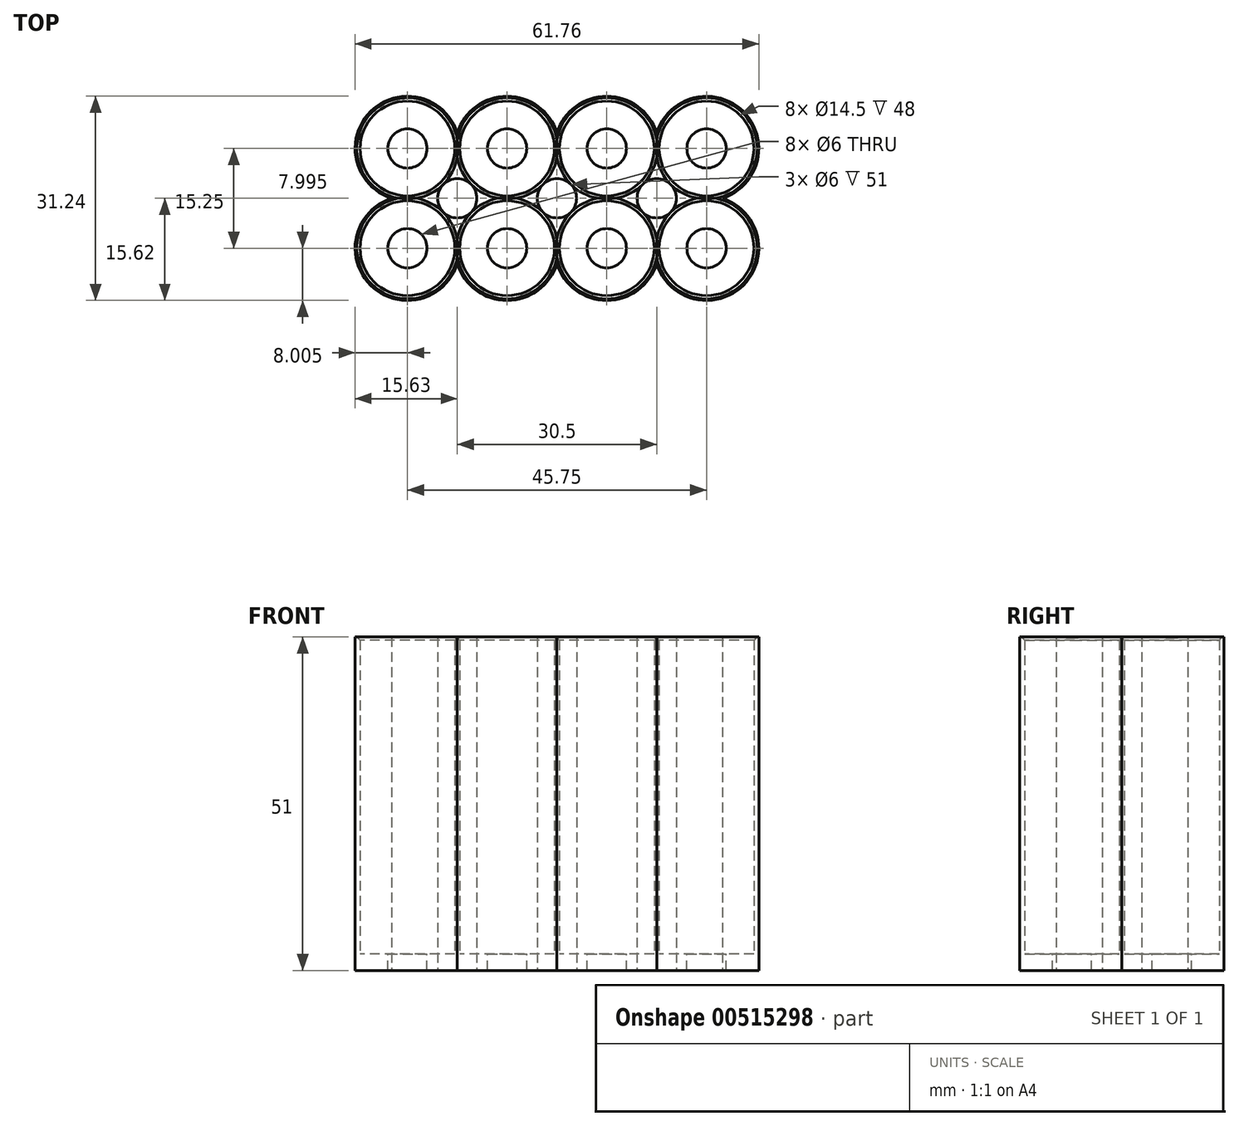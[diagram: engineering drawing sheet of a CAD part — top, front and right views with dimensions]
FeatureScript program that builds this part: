
annotation { "Feature Type Name" : "Feature", "Feature Type Description" : "" }
export const myFeature = defineFeature(function(context is Context, id is Id, definition is map)
    precondition{}
    {
        {
            var Q0;
            Q0=qCreatedBy(makeId("Top.planeOp"),FACE);
            var sketch = newSketch(context, id + "F0", { "sketchPlane" : qUnion([Q0])});
            skCircle(sketch, "E0", {"center": v(-7.62, 7.62) * mm, "radius": 7.25 * mm});
            skCircle(sketch, "E1", {"center": v(-22.88, 7.62) * mm, "radius": 7.25 * mm});
            skCircle(sketch, "E2.MirrorC", {"center": v(-7.62, -7.62) * mm, "radius": 7.25 * mm});
            skCircle(sketch, "E3.MirrorC", {"center": v(-22.88, -7.62) * mm, "radius": 7.25 * mm});
            skCircle(sketch, "E4.MirrorC", {"center": v(22.88, 7.62) * mm, "radius": 7.25 * mm});
            skCircle(sketch, "E5.MirrorC", {"center": v(7.62, 7.62) * mm, "radius": 7.25 * mm});
            skCircle(sketch, "E6.MirrorC", {"center": v(7.62, -7.62) * mm, "radius": 7.25 * mm});
            skCircle(sketch, "E7.MirrorC", {"center": v(22.88, -7.62) * mm, "radius": 7.25 * mm});
            skArc(sketch, "E8", {"start": v(25.3, 0) * mm, "mid": v(28.53, 13.28) * mm, "end": v(15.25, 10.05) * mm});
            skArc(sketch, "E9", {"start": v(15.25, -10.05) * mm, "mid": v(28.53, -13.28) * mm, "end": v(25.3, 0) * mm});
            skArc(sketch, "E10", {"start": v(0, -10.05) * mm, "mid": v(7.62, -15.62) * mm, "end": v(15.25, -10.05) * mm});
            skArc(sketch, "E11", {"start": v(15.25, 10.05) * mm, "mid": v(7.62, 15.62) * mm, "end": v(0, 10.05) * mm});
            skArc(sketch, "E12", {"start": v(0, 10.05) * mm, "mid": v(-7.62, 15.62) * mm, "end": v(-15.25, 10.05) * mm});
            skLineSegment(sketch, "E13", {"start": v(-15.25, -10.05) * mm, "end": v(-15.25, -10.05) * mm});
            skArc(sketch, "E14", {"start": v(-15.25, -10.05) * mm, "mid": v(-7.62, -15.62) * mm, "end": v(0, -10.05) * mm});
            skLineSegment(sketch, "E15", {"start": v(-25.3, 0) * mm, "end": v(-25.3, 0) * mm});
            skArc(sketch, "E16", {"start": v(-15.25, 10.05) * mm, "mid": v(-28.53, 13.28) * mm, "end": v(-25.3, 0) * mm});
            skArc(sketch, "E17", {"start": v(-25.3, 0) * mm, "mid": v(-28.53, -13.28) * mm, "end": v(-15.25, -10.05) * mm});
            skCircle(sketch, "E18", {"center": v(-15.25, 0) * mm, "radius": 3 * mm});
            skCircle(sketch, "E19", {"center": v(0, 0) * mm, "radius": 3 * mm});
            skCircle(sketch, "E20", {"center": v(15.25, 0) * mm, "radius": 3 * mm});
            skSolve(sketch);
        }
        {
            var Q0;
            Q0 = qSketchRegion(id + "F0", true);
            extrude(context, id + "F1", {"entities" : qUnion([Q0]), "depth" : 48.5 * mm, "offsetDistance" : 25 * mm});
        }
        {
            var Q0;
            Q0=makeQuery(id+"F1.opExtrude","CAP_FACE",FACE,{"disambiguationData":[OSD([sQuery(id+"F0.wireOp",EDGE,"E0"),sQuery(id+"F0.wireOp",EDGE,"E1"),sQuery(id+"F0.wireOp",EDGE,"E2.MirrorC"),sQuery(id+"F0.wireOp",EDGE,"E3.MirrorC"),sQuery(id+"F0.wireOp",EDGE,"E4.MirrorC"),sQuery(id+"F0.wireOp",EDGE,"E5.MirrorC"),sQuery(id+"F0.wireOp",EDGE,"E6.MirrorC"),sQuery(id+"F0.wireOp",EDGE,"E7.MirrorC"),sQuery(id+"F0.wireOp",EDGE,"E8"),sQuery(id+"F0.wireOp",EDGE,"E9"),sQuery(id+"F0.wireOp",EDGE,"E10"),sQuery(id+"F0.wireOp",EDGE,"E11"),sQuery(id+"F0.wireOp",EDGE,"E12"),sQuery(id+"F0.wireOp",EDGE,"E14"),sQuery(id+"F0.wireOp",EDGE,"E16"),sQuery(id+"F0.wireOp",EDGE,"E17"),sQuery(id+"F0.wireOp",EDGE,"E18"),sQuery(id+"F0.wireOp",EDGE,"E19"),sQuery(id+"F0.wireOp",EDGE,"E20")])],"isStart":true});
            var sketch = newSketch(context, id + "F2", { "sketchPlane" : qUnion([Q0])});
            skArc(sketch, "E21", {"start": v(-15.25, 10.05) * mm, "mid": v(-28.53, 13.28) * mm, "end": v(-25.3, 0) * mm});
            skArc(sketch, "E22", {"start": v(0, 10.05) * mm, "mid": v(-7.62, 15.62) * mm, "end": v(-15.25, 10.05) * mm});
            skArc(sketch, "E23", {"start": v(15.25, 10.05) * mm, "mid": v(7.62, 15.62) * mm, "end": v(0, 10.05) * mm});
            skArc(sketch, "E24", {"start": v(25.3, 0) * mm, "mid": v(28.53, 13.28) * mm, "end": v(15.25, 10.05) * mm});
            skArc(sketch, "E25", {"start": v(15.25, -10.05) * mm, "mid": v(28.53, -13.28) * mm, "end": v(25.3, 0) * mm});
            skArc(sketch, "E26", {"start": v(0, -10.05) * mm, "mid": v(7.62, -15.62) * mm, "end": v(15.25, -10.05) * mm});
            skArc(sketch, "E27", {"start": v(-15.25, -10.05) * mm, "mid": v(-7.62, -15.62) * mm, "end": v(0, -10.05) * mm});
            skArc(sketch, "E28", {"start": v(-25.3, 0) * mm, "mid": v(-28.53, -13.28) * mm, "end": v(-15.25, -10.05) * mm});
            skCircle(sketch, "E29", {"center": v(-15.25, 0) * mm, "radius": 3 * mm});
            skCircle(sketch, "E30", {"center": v(0, 0) * mm, "radius": 3 * mm});
            skCircle(sketch, "E31", {"center": v(15.25, 0) * mm, "radius": 3 * mm});
            skCircle(sketch, "E32", {"center": v(-22.88, 7.63) * mm, "radius": 3 * mm});
            skCircle(sketch, "E33", {"center": v(-7.62, 7.62) * mm, "radius": 3 * mm});
            skCircle(sketch, "E34", {"center": v(7.62, 7.62) * mm, "radius": 3 * mm});
            skCircle(sketch, "E35", {"center": v(22.88, 7.63) * mm, "radius": 3 * mm});
            skCircle(sketch, "E36", {"center": v(22.88, -7.63) * mm, "radius": 3 * mm});
            skCircle(sketch, "E37", {"center": v(7.62, -7.62) * mm, "radius": 3 * mm});
            skCircle(sketch, "E38", {"center": v(-7.63, -7.62) * mm, "radius": 3 * mm});
            skCircle(sketch, "E39", {"center": v(-22.88, -7.63) * mm, "radius": 3 * mm});
            skSolve(sketch);
        }
        {
            var Q0;
            Q0 = qSketchRegion(id + "F2", true);
            extrude(context, id + "F3", {"entities" : qUnion([Q0]), "operationType" : NewBodyOperationType.ADD, "depth" : 2.5 * mm, "offsetDistance" : 25 * mm});
        }
        {
            var Q0;
            Q0=makeQuery(id+"F1.opExtrude","CAP_EDGE",EDGE,{"disambiguationData":[OSD([sQuery(id+"F0.wireOp",EDGE,"E4.MirrorC")])],"isStart":false});
            var Q1;
            Q1=makeQuery(id+"F1.opExtrude","CAP_EDGE",EDGE,{"disambiguationData":[OSD([sQuery(id+"F0.wireOp",EDGE,"E5.MirrorC")])],"isStart":false});
            var Q2;
            Q2=makeQuery(id+"F1.opExtrude","CAP_EDGE",EDGE,{"disambiguationData":[OSD([sQuery(id+"F0.wireOp",EDGE,"E0")])],"isStart":false});
            var Q3;
            Q3=makeQuery(id+"F1.opExtrude","CAP_EDGE",EDGE,{"disambiguationData":[OSD([sQuery(id+"F0.wireOp",EDGE,"E1")])],"isStart":false});
            var Q4;
            Q4=makeQuery(id+"F1.opExtrude","CAP_EDGE",EDGE,{"disambiguationData":[OSD([sQuery(id+"F0.wireOp",EDGE,"E3.MirrorC")])],"isStart":false});
            var Q5;
            Q5=makeQuery(id+"F1.opExtrude","CAP_EDGE",EDGE,{"disambiguationData":[OSD([sQuery(id+"F0.wireOp",EDGE,"E2.MirrorC")])],"isStart":false});
            var Q6;
            Q6=makeQuery(id+"F1.opExtrude","CAP_EDGE",EDGE,{"disambiguationData":[OSD([sQuery(id+"F0.wireOp",EDGE,"E6.MirrorC")])],"isStart":false});
            var Q7;
            Q7=makeQuery(id+"F1.opExtrude","CAP_EDGE",EDGE,{"disambiguationData":[OSD([sQuery(id+"F0.wireOp",EDGE,"E7.MirrorC")])],"isStart":false});
            chamfer(context, id + "F4", {"entities" : qUnion([Q0, Q1, Q2, Q3, Q4, Q5, Q6, Q7]), "width" : .5 * mm, "tangentPropagation" : true});
        }
    });
